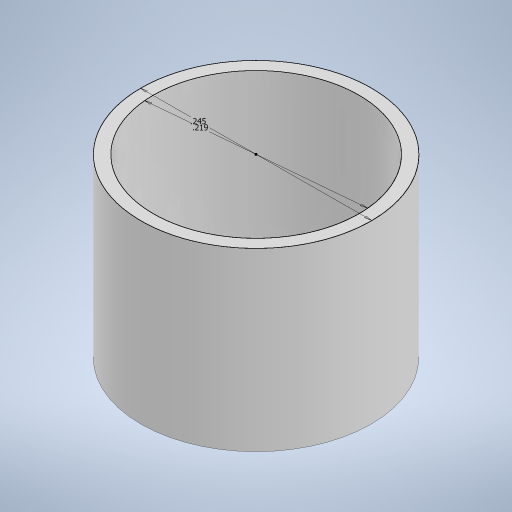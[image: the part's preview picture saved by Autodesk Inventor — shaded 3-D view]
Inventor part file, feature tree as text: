
AUTODESK INVENTOR PART (.ipt)
format: ipt  version: 2023 (Build 270158000, 158)  size: 196,096 bytes
history: native  units: in
note: dims shown in document units (in); Inventor stores cm internally (conversion verified against a paired STEP export)
features: extrude x2, sketch x1
ambient origin geometry x8: Origin, YZ Plane, XZ Plane, XY Plane, X Axis, Y Axis, Z Axis, Center Point
bodies: Solid1 (feature_tree)
feature tree (3):
  sketch  "Sketch1"  dims[d0=0.245in d1=0.2188in d2=0.1875in d3=0.0in d4=0.1562in d5=0.0in]
  extrude  "Extrusion1"  Depth=0.1562in
  extrude  "Extrusion2"  Depth=0.1875in TaperAngle=0.0deg
